# Revit family: Lighting_Desk-Table_Nordlux_Strap-16-Glass-Table
name_source: partatom
category: Lighting Fixtures
revit_build: Autodesk Revit 2018 (Build: 20170223_1515(x64)
units: mm (PartAtom-declared; Revit-internal decimal feet)

## family parameters
Always vertical = Yes
Cut with Voids When Loaded = No
Light Source = Yes
OmniClass Number = 23.35.47.11
OmniClass Title = Lighting Fixtures
Part Type = Normal
Room Calculation Point = No
Round Connector Dimension = Use Diameter
Shared = No
Work Plane-Based = Yes

## types (1)
- ART - (2020025001)
    Apparent Load = 7 VA
    BIMobject category = Desk & Table
    Beam angle = 109.50°
    Body material = Nordlux - Metal - Brushed steel
    CQS = 80.5
    CRI / Ra = 80.8
    Color Filter = 16777215
    Default Elevation = 1219.2 mm  [stored 4 ft]
    Description = With the frame made of brushed steel, the beautiful Strap table lamp combines raw leather and brushed steel with feminine opal glass in the finest way.
    Design country = Denmark
    Detail material = Nordlux - Metal - Brushed steel
    Dimming Lamp Color Temperature Shift = <None>
    EANNumber = 2020025001
    Edition number = 1
    Emit Shape Visible in Rendering = No
    Emit from Circle Diameter = 100 mm  [stored 0.328084 ft]
    Flicker frequency = 100 Hz
    IFC Classification = Light Fixture
    Installation instructions = https://asset.productmarketingcloud.com
    Manufacturer = Nordlux
    Manufacturer country = China
    Manufacturer name = Nordlux
    Material main = Metal
    Material secondary = Glass
    Model = Strap 16 Glass Table
    NominalVoltage = 230 V
    OmniClass Code = 23-35 47 11
    OmniClass Description = Lighting Fixtures
    Peak [cd] = 60.2
    Photometric Web File = Strap 16 Table Opalglass.ies
    Power factor = 0.59
    Product Guid = 9f9b2ec6-3456-4f78-ba02-1dc75505abab
    Product SKU = Strap-16-Glass-Table
    Product data url = https://bimobject.com
    Product family = Lighting
    Product group = Table
    Product name = Strap 16 Glass Table
    Product url = https://nordlux.com
    QR code = https://bimobject.com
    Shade material = Nordlux - Glass - Opalwh glass
    TM30 Rf = 83.4
    TM30 Rg = 95.5
    Tilt Angle = 90.00°
    URL = www.nordlux.com
    Weight Net (Kg) = 1,57
    Youtube clip = https://www.youtube.com

note: [stored X ft] marks values corroborated as IEEE doubles in the binary element streams (Revit-internal decimal feet)

## geometry (parser evidence)
native form markers: Sweep x3
no freeform markers — native parametric forms only
